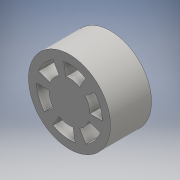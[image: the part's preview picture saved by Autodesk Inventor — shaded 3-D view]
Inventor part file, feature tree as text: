
AUTODESK INVENTOR PART (.ipt)
format: ipt  version: 2016 (Build 200138000, 138)  size: 130,560 bytes
history: native  units: mm
features: extrude x2, sketch x2, pattern_circular x1
ambient origin geometry x8: Origin, YZ Plane, XZ Plane, XY Plane, X Axis, Y Axis, Z Axis, Center Point
bodies: Solid1 (feature_tree)
feature tree (5):
  extrude  "Extrusion1"  Depth=10.0mm TaperAngle=0.0deg
  extrude  "Extrusion2"  Depth=5.0mm
  pattern_circular  "Circular Pattern1"  [2 undecoded]
  sketch  "Sketch1"  dims[d0=20.0mm d1=10.0mm d2=0.0mm]
  sketch  "Sketch2"  dims[d3=6.981317mm d4=5.0mm d5=8.0mm d6=10.0mm d7=0.0mm d8=60.0mm d9=360.0deg]
note: 2 required parameter values undecoded (feature->parameter linkage not recoverable at this tier; creation-order binding heuristic only, values carry confidence <= 0.55)
